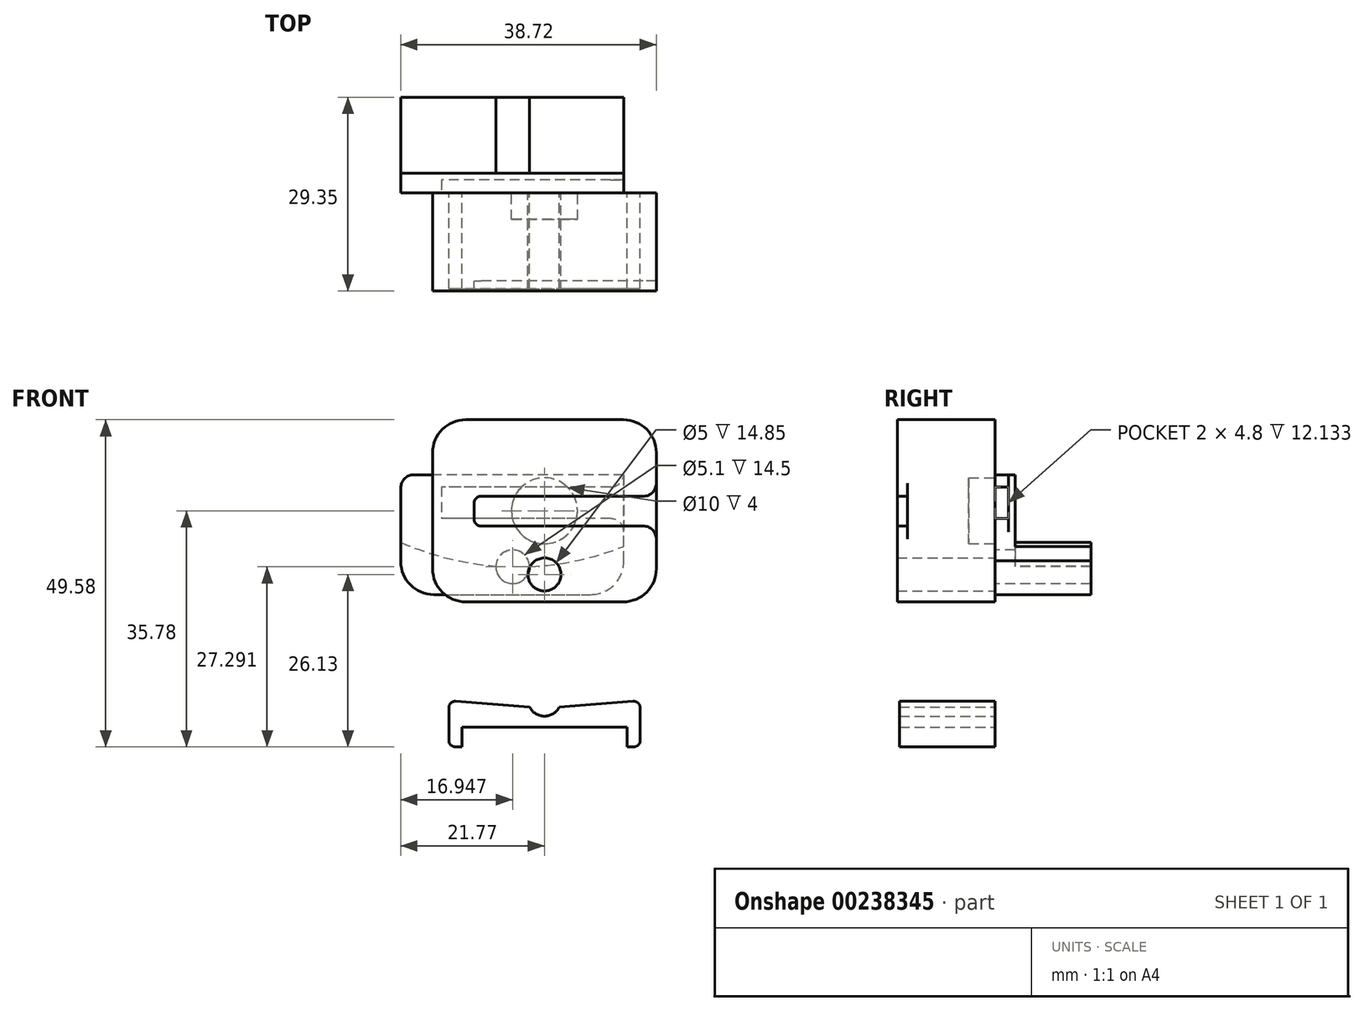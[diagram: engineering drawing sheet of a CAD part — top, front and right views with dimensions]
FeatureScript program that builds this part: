
annotation { "Feature Type Name" : "Feature", "Feature Type Description" : "" }
export const myFeature = defineFeature(function(context is Context, id is Id, definition is map)
    precondition{}
    {
        {
            var Q0;
            Q0=qCreatedBy(makeId("Front.planeOp"),FACE);
            var sketch = newSketch(context, id + "F0", { "sketchPlane" : qUnion([Q0])});
            skLineSegment(sketch, "E0.bottom", {"start": v(-11.95, 13.8) * mm, "end": v(11.95, 13.8) * mm});
            skLineSegment(sketch, "E0.top", {"start": v(-11.95, -13.8) * mm, "end": v(11.95, -13.8) * mm});
            skLineSegment(sketch, "E0.left", {"start": v(-16.95, 8.8) * mm, "end": v(-16.95, -8.8) * mm});
            skLineSegment(sketch, "E0.right", {"start": v(16.95, 8.8) * mm, "end": v(16.95, 4.2) * mm});
            skPoint(sketch, "E0.middle", {"position": v(0, 0) * mm});
            skPoint(sketch, "E1.orphan", {"position": v(16.95, 13.8) * mm});
            skPoint(sketch, "E2.orphan", {"position": v(16.95, -13.8) * mm});
            skPoint(sketch, "E3.orphan", {"position": v(-16.95, -13.8) * mm});
            skPoint(sketch, "E4.orphan", {"position": v(-16.95, 13.8) * mm});
            skArc(sketch, "E5.filletArc", {"start": v(-11.95, 13.8) * mm, "mid": v(-15.49, 12.34) * mm, "end": v(-16.95, 8.8) * mm});
            skArc(sketch, "E6.filletArc", {"start": v(-16.95, -8.8) * mm, "mid": v(-15.49, -12.34) * mm, "end": v(-11.95, -13.8) * mm});
            skArc(sketch, "E7.filletArc", {"start": v(11.95, -13.8) * mm, "mid": v(15.49, -12.34) * mm, "end": v(16.95, -8.8) * mm});
            skArc(sketch, "E8.filletArc", {"start": v(16.95, 8.8) * mm, "mid": v(15.49, 12.34) * mm, "end": v(11.95, 13.8) * mm});
            skCircle(sketch, "E9", {"center": v(0, -9.65) * mm, "radius": 2.5 * mm});
            skLineSegment(sketch, "E10.bottom", {"start": v(14.95, 2.2) * mm, "end": v(-10.65, 2.2) * mm});
            skLineSegment(sketch, "E10.top", {"start": v(14.95, -2.3) * mm, "end": v(-10.65, -2.3) * mm});
            skLineSegment(sketch, "E10.left", {"start": v(16.95, 2.2) * mm, "end": v(16.95, -2.3) * mm});
            skLineSegment(sketch, "E10.right", {"start": v(-10.65, 2.2) * mm, "end": v(-10.65, -2.3) * mm});
            skPoint(sketch, "E11", {"position": v(16.95, 2.3) * mm});
            skPoint(sketch, "E12", {"position": v(16.95, -2.3) * mm});
            skArc(sketch, "E13.filletArc", {"start": v(14.95, 2.2) * mm, "mid": v(16.36, 2.79) * mm, "end": v(16.95, 4.2) * mm});
            skLineSegment(sketch, "E14", {"start": v(16.95, -8.8) * mm, "end": v(16.95, -4.3) * mm});
            skArc(sketch, "E15.filletArc", {"start": v(16.95, -4.3) * mm, "mid": v(16.36, -2.89) * mm, "end": v(14.95, -2.3) * mm});
            skLineSegment(sketch, "E16", {"start": v(16.95, 4.2) * mm, "end": v(16.95, 2.2) * mm});
            skLineSegment(sketch, "E17", {"start": v(16.95, -2.3) * mm, "end": v(16.95, -4.3) * mm});
            skCircle(sketch, "E18", {"center": v(0, 0) * mm, "radius": 5 * mm});
            skArc(sketch, "E19", {"start": v(-16.95, -5.89) * mm, "mid": v(-0.07, -9.65) * mm, "end": v(16.95, -6.55) * mm});
            skPoint(sketch, "E19.second.point", {"position": v(-16.95, -5.89) * mm});
            skPoint(sketch, "E19.third.point", {"position": v(16.95, -6.55) * mm});
            skSolve(sketch);
        }
        {
            var Q0;
            Q0=makeQuery(id+"F0.imprint","IMPRINT",FACE,{"disambiguationData":[TD([[makeQuery(id+"F0.imprint","IMPRINT",EDGE,{"derivedFrom":sQuery(id+"F0.wireOp",EDGE,"E0.bottom")}),-1.0]])]});
            var Q1;
            Q1=makeQuery(id+"F0.imprint","IMPRINT",FACE,{"disambiguationData":[TD([[makeQuery(id+"F0.imprint","IMPRINT",EDGE,{"derivedFrom":sQuery(id+"F0.wireOp",EDGE,"E0.top")}),1.0]])]});
            extrude(context, id + "F1", {"entities" : qUnion([Q0, Q1]), "depth" : 14.85 * mm});
        }
        {
            var Q0;
            {var subQ0=sQuery(id+"F0.wireOp",EDGE,"E10.right");Q0=makeQuery(id+"F0.imprint","IMPRINT",FACE,{"disambiguationData":[TD([[makeQuery(id+"F0.imprint","IMPRINT",EDGE,{"derivedFrom":subQ0}),1.0]])]});}
            var Q1;
            {var subQ0=sQuery(id+"F0.wireOp",EDGE,"E18");var subQ1=sQuery(id+"F0.wireOp",EDGE,"E10.bottom");var subQ2=makeQuery(id+"F0.imprint","INTERSECT",VERTEX,{"disambiguationData":[OD(0.0)],"derivedFrom":[subQ1,subQ0]});Q1=makeQuery(id+"F0.imprint","IMPRINT",FACE,{"disambiguationData":[TD([[makeQuery(id+"F0.imprint","IMPRINT",EDGE,{"disambiguationData":[TD([[subQ2,-1.0]])],"derivedFrom":subQ1}),1.0]])]});}
            var Q2;
            Q2=makeQuery(id+"F0.imprint","IMPRINT",FACE,{"disambiguationData":[TD([[makeQuery(id+"F0.imprint","IMPRINT",EDGE,{"derivedFrom":sQuery(id+"F0.wireOp",EDGE,"E10.left")}),-1.0]])]});
            extrude(context, id + "F2", {"entities" : qUnion([Q0, Q1, Q2]), "operationType" : NewBodyOperationType.ADD, "depth" : 13.3 * mm});
        }
        {
            var Q0;
            {var subQ0=sQuery(id+"F0.wireOp",EDGE,"E18");var subQ1=sQuery(id+"F0.wireOp",EDGE,"E10.bottom");var subQ2=makeQuery(id+"F0.imprint","INTERSECT",VERTEX,{"disambiguationData":[OD(0.0)],"derivedFrom":[subQ1,subQ0]});Q0=makeQuery(id+"F0.imprint","IMPRINT",FACE,{"disambiguationData":[TD([[makeQuery(id+"F0.imprint","IMPRINT",EDGE,{"disambiguationData":[TD([[subQ2,-1.0]])],"derivedFrom":subQ1}),-1.0]])]});}
            var Q1;
            {var subQ0=sQuery(id+"F0.wireOp",EDGE,"E18");var subQ1=sQuery(id+"F0.wireOp",EDGE,"E10.top");var subQ2=makeQuery(id+"F0.imprint","INTERSECT",VERTEX,{"disambiguationData":[OD(0.0)],"derivedFrom":[subQ1,subQ0]});Q1=makeQuery(id+"F0.imprint","IMPRINT",FACE,{"disambiguationData":[TD([[makeQuery(id+"F0.imprint","IMPRINT",EDGE,{"disambiguationData":[TD([[subQ2,-1.0]])],"derivedFrom":subQ1}),1.0]])]});}
            var Q2;
            {var subQ0=sQuery(id+"F0.wireOp",EDGE,"E18");var subQ1=sQuery(id+"F0.wireOp",EDGE,"E10.bottom");var subQ2=makeQuery(id+"F0.imprint","INTERSECT",VERTEX,{"disambiguationData":[OD(0.0)],"derivedFrom":[subQ1,subQ0]});Q2=makeQuery(id+"F0.imprint","IMPRINT",FACE,{"disambiguationData":[TD([[makeQuery(id+"F0.imprint","IMPRINT",EDGE,{"disambiguationData":[TD([[subQ2,-1.0]])],"derivedFrom":subQ1}),1.0]])]});}
            extrude(context, id + "F3", {"entities" : qUnion([Q0, Q1, Q2]), "operationType" : NewBodyOperationType.ADD, "depth" : 13.3 * mm, "hasSecondDirection" : true, "secondDirectionOppositeDirection" : false, "secondDirectionDepth" : 4 * mm});
        }
        {
            var Q0;
            {var subQ0=sQuery(id+"F0.wireOp",EDGE,"E18");var subQ1=sQuery(id+"F0.wireOp",EDGE,"E10.bottom");var subQ2=makeQuery(id+"F0.imprint","INTERSECT",VERTEX,{"disambiguationData":[OD(0.0)],"derivedFrom":[subQ1,subQ0]});Q0=makeQuery(id+"F0.imprint","IMPRINT",FACE,{"disambiguationData":[TD([[makeQuery(id+"F0.imprint","IMPRINT",EDGE,{"disambiguationData":[TD([[subQ2,-1.0]])],"derivedFrom":subQ1}),1.0]])]});}
            extrude(context, id + "F4", {"entities" : qUnion([Q0]), "operationType" : NewBodyOperationType.REMOVE, "depth" : 4 * mm});
        }
        {
            var Q0;
            {var subQ0=sQuery(id+"F0.wireOp",EDGE,"E18");var subQ1=sQuery(id+"F0.wireOp",EDGE,"E10.bottom");var subQ2=makeQuery(id+"F0.imprint","INTERSECT",VERTEX,{"disambiguationData":[OD(0.0)],"derivedFrom":[subQ1,subQ0]});Q0=makeQuery(id+"F0.imprint","IMPRINT",FACE,{"disambiguationData":[TD([[makeQuery(id+"F0.imprint","IMPRINT",EDGE,{"disambiguationData":[TD([[subQ2,-1.0]])],"derivedFrom":subQ1}),-1.0]])]});}
            var Q1;
            {var subQ0=sQuery(id+"F0.wireOp",EDGE,"E18");var subQ1=sQuery(id+"F0.wireOp",EDGE,"E10.top");var subQ2=makeQuery(id+"F0.imprint","INTERSECT",VERTEX,{"disambiguationData":[OD(0.0)],"derivedFrom":[subQ1,subQ0]});Q1=makeQuery(id+"F0.imprint","IMPRINT",FACE,{"disambiguationData":[TD([[makeQuery(id+"F0.imprint","IMPRINT",EDGE,{"disambiguationData":[TD([[subQ2,-1.0]])],"derivedFrom":subQ1}),1.0]])]});}
            extrude(context, id + "F5", {"entities" : qUnion([Q0, Q1]), "operationType" : NewBodyOperationType.ADD, "depth" : 14.85 * mm, "hasSecondDirection" : true, "secondDirectionOppositeDirection" : false, "secondDirectionDepth" : 4 * mm});
        }
        {
            var Q0;
            Q0=makeQuery(id+"F1.opExtrude","SWEPT_EDGE",EDGE,{"disambiguationData":[OSD([sQuery(id+"F0.wireOp",EDGE,"E10.bottom"),sQuery(id+"F0.wireOp",EDGE,"E10.right")])]});
            var Q1;
            Q1=makeQuery(id+"F1.opExtrude","SWEPT_EDGE",EDGE,{"disambiguationData":[OSD([sQuery(id+"F0.wireOp",EDGE,"E10.top"),sQuery(id+"F0.wireOp",EDGE,"E10.right")])]});
            fillet(context, id + "F6", {"entities" : qUnion([Q0, Q1]), "radius" : 1 * mm, "tangentPropagation" : true, "allowEdgeOverflow" : false});
        }
        {
            var Q0;
            Q0=qCreatedBy(makeId("Front.planeOp"),FACE);
            var sketch = newSketch(context, id + "F7", { "sketchPlane" : qUnion([Q0])});
            skLineSegment(sketch, "E20.top", {"start": v(-16.77, -12.69) * mm, "end": v(7.01, -12.69) * mm});
            skLineSegment(sketch, "E20.left", {"start": v(-21.77, 3.46) * mm, "end": v(-21.77, -7.69) * mm});
            skPoint(sketch, "E20.middle", {"position": v(-4.82, 1.11) * mm});
            skPoint(sketch, "E21.orphan", {"position": v(12.13, 14.91) * mm});
            skPoint(sketch, "E22.orphan", {"position": v(12.13, -12.69) * mm});
            skPoint(sketch, "E23.orphan", {"position": v(-21.77, -12.69) * mm});
            skPoint(sketch, "E24.orphan", {"position": v(-21.77, 14.91) * mm});
            skArc(sketch, "E25.filletArc", {"start": v(-21.77, -7.69) * mm, "mid": v(-20.3, -11.22) * mm, "end": v(-16.77, -12.69) * mm});
            skArc(sketch, "E26.filletArc", {"start": v(7.01, -12.69) * mm, "mid": v(10.58, -11.19) * mm, "end": v(12, -7.58) * mm});
            skCircle(sketch, "E27", {"center": v(-4.82, -8.49) * mm, "radius": 2.55 * mm});
            skLineSegment(sketch, "E28.bottom", {"start": v(10.02, 3.61) * mm, "end": v(-15.6, 3.61) * mm});
            skLineSegment(sketch, "E28.top", {"start": v(10, -1.19) * mm, "end": v(-15.6, -1.19) * mm});
            skLineSegment(sketch, "E28.left", {"start": v(12, 3.31) * mm, "end": v(12, -1.19) * mm});
            skLineSegment(sketch, "E28.right", {"start": v(-15.6, 3.61) * mm, "end": v(-15.6, -1.19) * mm});
            skPoint(sketch, "E29", {"position": v(12.13, 3.41) * mm});
            skPoint(sketch, "E30", {"position": v(12, -1.19) * mm});
            skArc(sketch, "E31.filletArc", {"start": v(10.02, 3.61) * mm, "mid": v(11.38, 4.15) * mm, "end": v(12, 5.46) * mm});
            skLineSegment(sketch, "E32", {"start": v(12, -7.58) * mm, "end": v(12, -3.19) * mm});
            skArc(sketch, "E33.filletArc", {"start": v(12, -3.19) * mm, "mid": v(11.42, -1.77) * mm, "end": v(10, -1.19) * mm});
            skLineSegment(sketch, "E34", {"start": v(12, 5.46) * mm, "end": v(12, 3.31) * mm});
            skLineSegment(sketch, "E35", {"start": v(12, -1.19) * mm, "end": v(12, -3.19) * mm});
            skArc(sketch, "E36", {"start": v(-21.77, -4.78) * mm, "mid": v(-4.94, -8.49) * mm, "end": v(12, -5.39) * mm});
            skPoint(sketch, "E36.second.point", {"position": v(-21.77, -4.78) * mm});
            skPoint(sketch, "E36.third.point", {"position": v(12, -5.39) * mm});
            skLineSegment(sketch, "E37", {"start": v(12, 5.46) * mm, "end": v(-19.77, 5.46) * mm});
            skPoint(sketch, "E38.visualSharp", {"position": v(-21.77, 5.46) * mm});
            skArc(sketch, "E38.filletArc", {"start": v(-19.77, 5.46) * mm, "mid": v(-21.19, 4.88) * mm, "end": v(-21.77, 3.46) * mm});
            skSolve(sketch);
        }
        {
            var Q0;
            Q0=makeQuery(id+"F7.imprint","IMPRINT",FACE,{"disambiguationData":[TD([[makeQuery(id+"F7.imprint","IMPRINT",EDGE,{"derivedFrom":sQuery(id+"F7.wireOp",EDGE,"E20.top")}),1.0]])]});
            extrude(context, id + "F8", {"entities" : qUnion([Q0]), "oppositeDirection" : true, "depth" : 14.5 * mm});
        }
        {
            var Q0;
            Q0=makeQuery(id+"F7.imprint","IMPRINT",FACE,{"disambiguationData":[TD([[makeQuery(id+"F7.imprint","IMPRINT",EDGE,{"derivedFrom":sQuery(id+"F7.wireOp",EDGE,"E28.bottom")}),-1.0]])]});
            var Q1;
            Q1=makeQuery(id+"F7.imprint","IMPRINT",FACE,{"disambiguationData":[TD([[makeQuery(id+"F7.imprint","IMPRINT",EDGE,{"derivedFrom":sQuery(id+"F7.wireOp",EDGE,"E28.bottom")}),1.0]])]});
            extrude(context, id + "F9", {"entities" : qUnion([Q0, Q1]), "operationType" : NewBodyOperationType.ADD, "oppositeDirection" : true, "depth" : 3 * mm});
        }
        {
            var Q0;
            Q0=makeQuery(id+"F7.imprint","IMPRINT",FACE,{"disambiguationData":[TD([[makeQuery(id+"F7.imprint","IMPRINT",EDGE,{"derivedFrom":sQuery(id+"F7.wireOp",EDGE,"E28.bottom")}),1.0]])]});
            extrude(context, id + "F10", {"entities" : qUnion([Q0]), "operationType" : NewBodyOperationType.REMOVE, "oppositeDirection" : true, "depth" : 2 * mm});
        }
        {
            var Q0;
            Q0=qCreatedBy(makeId("Front.planeOp"),FACE);
            var sketch = newSketch(context, id + "F11", { "sketchPlane" : qUnion([Q0])});
            skLineSegment(sketch, "E39", {"start": v(0, -32.78) * mm, "end": v(12.5, -32.78) * mm});
            skLineSegment(sketch, "E40", {"start": v(0, -32.78) * mm, "end": v(-12.5, -32.78) * mm});
            skLineSegment(sketch, "E41", {"start": v(-12.5, -32.78) * mm, "end": v(-12.5, -35.78) * mm});
            skLineSegment(sketch, "E42", {"start": v(-12.5, -35.78) * mm, "end": v(-13.5, -35.78) * mm});
            skLineSegment(sketch, "E43", {"start": v(-14.5, -34.78) * mm, "end": v(-14.5, -29.86) * mm});
            skLineSegment(sketch, "E44", {"start": v(14.5, -29.86) * mm, "end": v(14.5, -34.78) * mm});
            skLineSegment(sketch, "E45", {"start": v(13.5, -35.78) * mm, "end": v(12.5, -35.78) * mm});
            skLineSegment(sketch, "E46", {"start": v(12.5, -35.78) * mm, "end": v(12.5, -32.78) * mm});
            skPoint(sketch, "E47.endSnap0", {"position": v(0, -28.78) * mm});
            skArc(sketch, "E48", {"start": v(-2.26, -29.7) * mm, "mid": v(0, -31.13) * mm, "end": v(2.26, -29.7) * mm});
            skPoint(sketch, "E49", {"position": v(0, -29.88) * mm});
            skLineSegment(sketch, "E50", {"start": v(-13.42, -28.86) * mm, "end": v(-2.26, -29.7) * mm});
            skLineSegment(sketch, "E51", {"start": v(13.42, -28.86) * mm, "end": v(2.26, -29.7) * mm});
            skPoint(sketch, "E52.visualSharp", {"position": v(-14.5, -28.78) * mm});
            skArc(sketch, "E52.filletArc", {"start": v(-13.42, -28.86) * mm, "mid": v(-14.18, -29.13) * mm, "end": v(-14.5, -29.86) * mm});
            skPoint(sketch, "E53.visualSharp", {"position": v(14.5, -28.78) * mm});
            skArc(sketch, "E53.filletArc", {"start": v(14.5, -29.86) * mm, "mid": v(14.18, -29.13) * mm, "end": v(13.42, -28.86) * mm});
            skPoint(sketch, "E54.visualSharp", {"position": v(14.5, -35.78) * mm});
            skArc(sketch, "E54.filletArc", {"start": v(13.5, -35.78) * mm, "mid": v(14.2, -35.49) * mm, "end": v(14.5, -34.78) * mm});
            skPoint(sketch, "E55.visualSharp", {"position": v(-14.5, -35.78) * mm});
            skArc(sketch, "E55.filletArc", {"start": v(-14.5, -34.78) * mm, "mid": v(-14.2, -35.49) * mm, "end": v(-13.5, -35.78) * mm});
            skPoint(sketch, "E56.end.orphan", {"position": v(0, -31.13) * mm});
            skSolve(sketch);
        }
        {
            var Q0;
            Q0=makeQuery(id+"F11.imprint","IMPRINT",FACE,{"disambiguationData":[TD([[makeQuery(id+"F11.imprint","IMPRINT",EDGE,{"derivedFrom":sQuery(id+"F11.wireOp",EDGE,"E39")}),1.0]])]});
            extrude(context, id + "F12", {"entities" : qUnion([Q0]), "depth" : 14.5 * mm});
        }
    });
